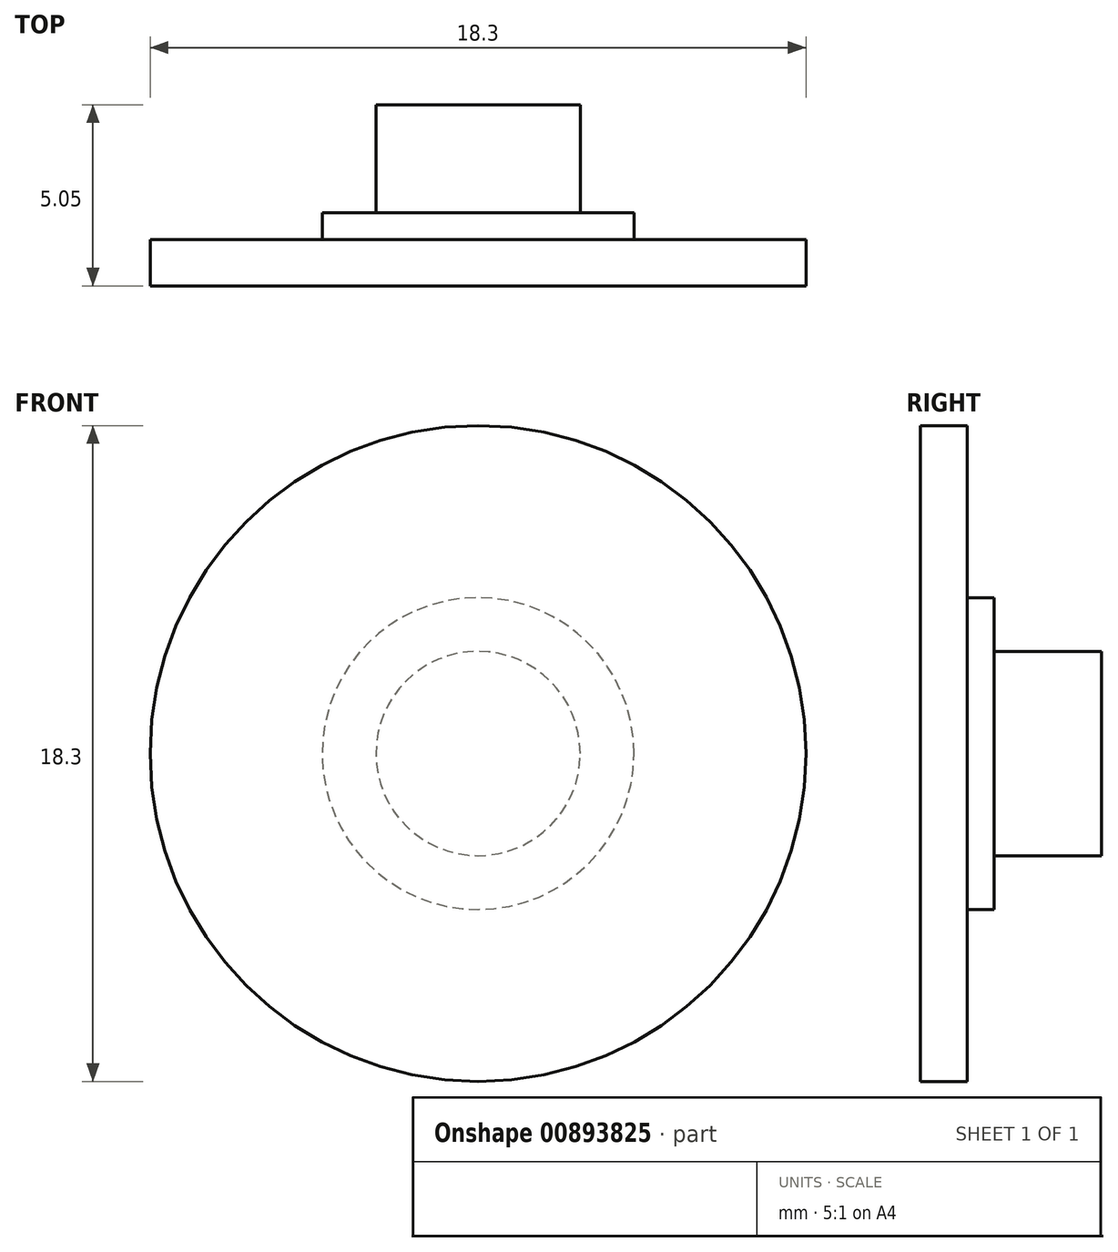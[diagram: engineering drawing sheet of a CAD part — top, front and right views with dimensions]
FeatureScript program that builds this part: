
annotation { "Feature Type Name" : "Feature", "Feature Type Description" : "" }
export const myFeature = defineFeature(function(context is Context, id is Id, definition is map)
    precondition{}
    {
        {
            var Q0;
            Q0=qCreatedBy(makeId("Top.planeOp"),FACE);
            var sketch = newSketch(context, id + "F0", { "sketchPlane" : qUnion([Q0])});
            skLineSegment(sketch, "E0", {"start": v(0, 0) * mm, "end": v(0, 10.51) * mm, "construction": true});
            skLineSegment(sketch, "E1", {"start": v(2.85, 10.75) * mm, "end": v(2.85, 7.75) * mm});
            skLineSegment(sketch, "E2", {"start": v(2.85, 7.75) * mm, "end": v(4.35, 7.75) * mm});
            skLineSegment(sketch, "E3", {"start": v(4.35, 7.75) * mm, "end": v(4.35, 7) * mm});
            skLineSegment(sketch, "E4", {"start": v(4.35, 7) * mm, "end": v(9.15, 7) * mm});
            skLineSegment(sketch, "E5", {"start": v(9.15, 7) * mm, "end": v(9.15, 5.7) * mm});
            skLineSegment(sketch, "E6", {"start": v(9.15, 5.7) * mm, "end": v(0, 5.7) * mm});
            skLineSegment(sketch, "E7", {"start": v(2.85, 10.75) * mm, "end": v(0, 10.75) * mm});
            skSolve(sketch);
        }
        {
            var Q0;
            Q0=sQuery(id+"F0.wireOp",EDGE,"E2");
            var Q1;
            Q1=sQuery(id+"F0.wireOp",EDGE,"E4");
            var Q2;
            Q2=sQuery(id+"F0.wireOp",EDGE,"E3");
            var Q3;
            Q3=sQuery(id+"F0.wireOp",EDGE,"E6");
            var Q4;
            Q4=sQuery(id+"F0.wireOp",EDGE,"E5");
            var Q5;
            Q5=sQuery(id+"F0.wireOp",EDGE,"E1");
            var Q6;
            Q6=sQuery(id+"F0.wireOp",EDGE,"E7");
            var Q7;
            Q7=sQuery(id+"F0.wireOp",EDGE,"E0");
            revolve(context, id + "F1", {"bodyType" : ToolBodyType.SURFACE, "surfaceOperationType" : NewSurfaceOperationType.NEW, "surfaceEntities" : qUnion([Q0, Q1, Q2, Q3, Q4, Q5, Q6]), "axis" : qUnion([Q7]), "revolveType" : RevolveType.FULL});
        }
    });
